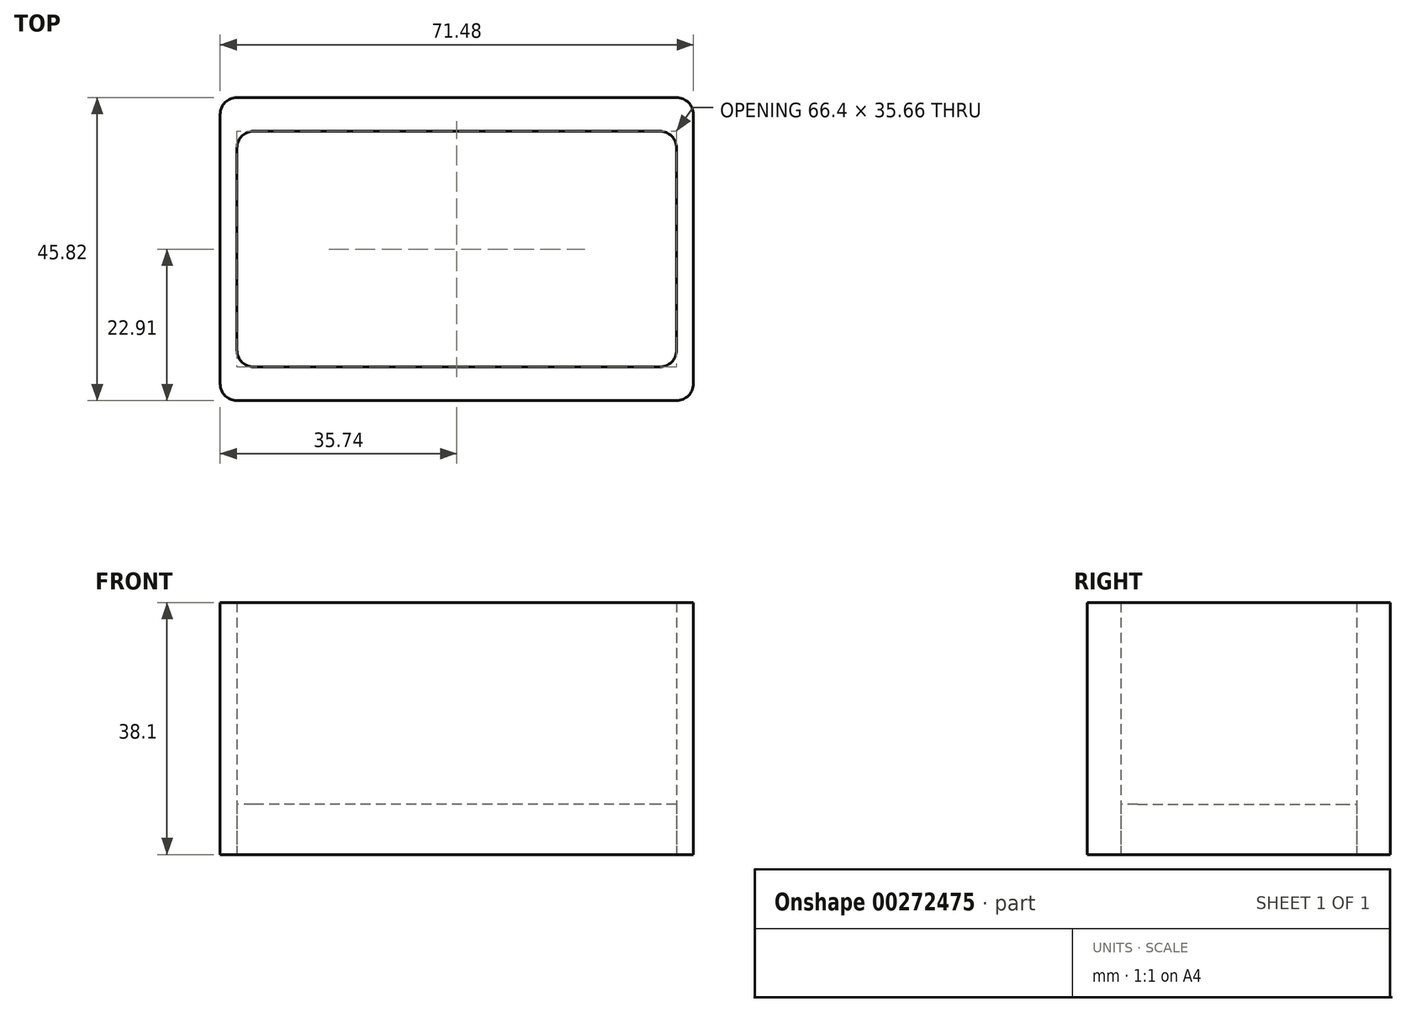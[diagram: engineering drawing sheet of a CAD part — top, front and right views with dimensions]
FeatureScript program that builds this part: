
annotation { "Feature Type Name" : "Feature", "Feature Type Description" : "" }
export const myFeature = defineFeature(function(context is Context, id is Id, definition is map)
    precondition{}
    {
        {
            var Q0;
            Q0=qCreatedBy(makeId("Top.planeOp"),FACE);
            var sketch = newSketch(context, id + "F0", { "sketchPlane" : qUnion([Q0])});
            skLineSegment(sketch, "E0.bottom", {"start": v(30.66, -17.83) * mm, "end": v(-30.66, -17.83) * mm});
            skLineSegment(sketch, "E0.top", {"start": v(30.66, 17.83) * mm, "end": v(-30.66, 17.83) * mm});
            skLineSegment(sketch, "E0.left", {"start": v(33.2, -15.29) * mm, "end": v(33.2, 15.29) * mm});
            skLineSegment(sketch, "E0.right", {"start": v(-33.2, -15.29) * mm, "end": v(-33.2, 15.29) * mm});
            skPoint(sketch, "E0.middle", {"position": v(0, 0) * mm});
            skPoint(sketch, "E1.visualSharp", {"position": v(-33.2, 17.83) * mm});
            skArc(sketch, "E1.filletArc", {"start": v(-30.66, 17.83) * mm, "mid": v(-32.46, 17.08) * mm, "end": v(-33.2, 15.29) * mm});
            skPoint(sketch, "E2.visualSharp", {"position": v(33.2, -17.83) * mm});
            skArc(sketch, "E2.filletArc", {"start": v(30.66, -17.83) * mm, "mid": v(32.46, -17.08) * mm, "end": v(33.2, -15.29) * mm});
            skPoint(sketch, "E3.visualSharp", {"position": v(33.2, 17.83) * mm});
            skArc(sketch, "E3.filletArc", {"start": v(33.2, 15.29) * mm, "mid": v(32.46, 17.08) * mm, "end": v(30.66, 17.83) * mm});
            skPoint(sketch, "E4.visualSharp", {"position": v(-33.2, -17.83) * mm});
            skArc(sketch, "E4.filletArc", {"start": v(-33.2, -15.29) * mm, "mid": v(-32.46, -17.08) * mm, "end": v(-30.66, -17.83) * mm});
            skLineSegment(sketch, "E5.bottom", {"start": v(33.2, -22.9) * mm, "end": v(-33.2, -22.9) * mm});
            skLineSegment(sketch, "E5.top", {"start": v(33.2, 22.9) * mm, "end": v(-33.2, 22.9) * mm});
            skLineSegment(sketch, "E5.left", {"start": v(35.74, -20.37) * mm, "end": v(35.74, 20.37) * mm});
            skLineSegment(sketch, "E5.right", {"start": v(-35.74, -20.37) * mm, "end": v(-35.74, 20.37) * mm});
            skPoint(sketch, "E6.visualSharp", {"position": v(35.74, 22.9) * mm});
            skArc(sketch, "E6.filletArc", {"start": v(35.74, 20.37) * mm, "mid": v(35, 22.16) * mm, "end": v(33.2, 22.9) * mm});
            skPoint(sketch, "E7.visualSharp", {"position": v(35.74, -22.9) * mm});
            skArc(sketch, "E7.filletArc", {"start": v(33.2, -22.9) * mm, "mid": v(35, -22.16) * mm, "end": v(35.74, -20.37) * mm});
            skPoint(sketch, "E8.visualSharp", {"position": v(-35.74, -22.9) * mm});
            skArc(sketch, "E8.filletArc", {"start": v(-35.74, -20.37) * mm, "mid": v(-35, -22.16) * mm, "end": v(-33.2, -22.9) * mm});
            skPoint(sketch, "E9.visualSharp", {"position": v(-35.74, 22.9) * mm});
            skArc(sketch, "E9.filletArc", {"start": v(-33.2, 22.9) * mm, "mid": v(-35, 22.16) * mm, "end": v(-35.74, 20.37) * mm});
            skSolve(sketch);
        }
        {
            var Q0;
            Q0=makeQuery(id+"F0.imprint","IMPRINT",FACE,{"disambiguationData":[TD([[makeQuery(id+"F0.imprint","IMPRINT",EDGE,{"derivedFrom":sQuery(id+"F0.wireOp",EDGE,"E0.bottom")}),-1.0]])]});
            extrude(context, id + "F1", {"entities" : qUnion([Q0]), "depth" : 7.62 * mm});
        }
        {
            var Q0;
            Q0=makeQuery(id+"F0.imprint","IMPRINT",FACE,{"disambiguationData":[TD([[makeQuery(id+"F0.imprint","IMPRINT",EDGE,{"derivedFrom":sQuery(id+"F0.wireOp",EDGE,"E0.bottom")}),1.0]])]});
            extrude(context, id + "F2", {"entities" : qUnion([Q0]), "depth" : 38.1 * mm});
        }
    });
